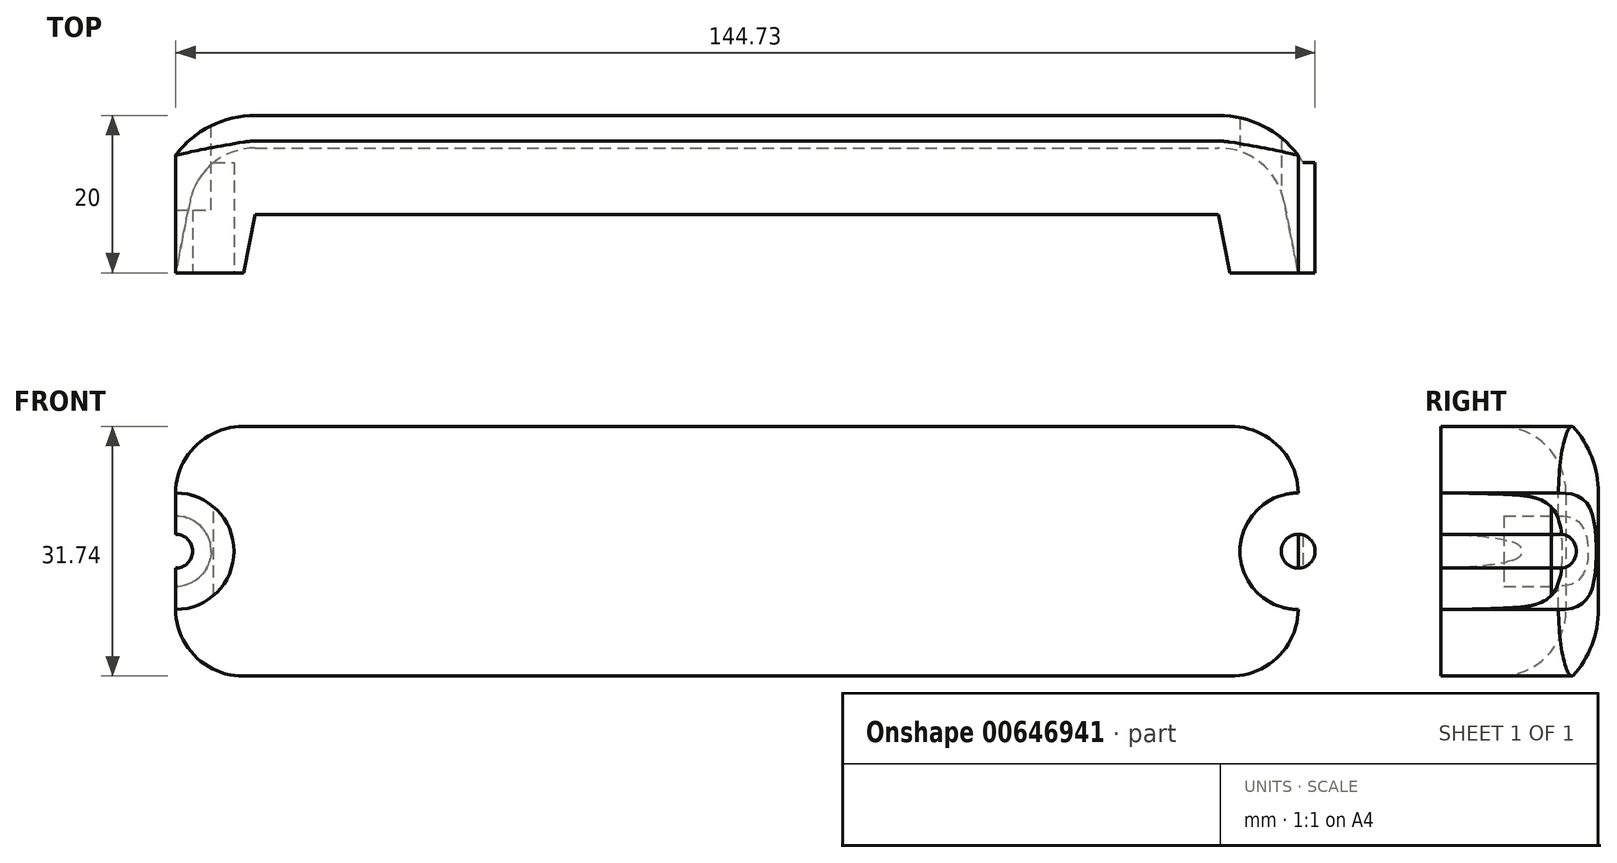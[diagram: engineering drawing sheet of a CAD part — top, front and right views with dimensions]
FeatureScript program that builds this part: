
annotation { "Feature Type Name" : "Feature", "Feature Type Description" : "" }
export const myFeature = defineFeature(function(context is Context, id is Id, definition is map)
    precondition{}
    {
        {
            var Q0;
            Q0=qCreatedBy(makeId("Top.planeOp"),FACE);
            var sketch = newSketch(context, id + "F0", { "sketchPlane" : qUnion([Q0])});
            skLineSegment(sketch, "E0.bottom", {"start": v(75.5, -10) * mm, "end": v(-75.5, -10) * mm});
            skLineSegment(sketch, "E0.top", {"start": v(75.5, 10) * mm, "end": v(-75.5, 10) * mm});
            skLineSegment(sketch, "E0.left", {"start": v(75.5, -10) * mm, "end": v(75.5, 10) * mm});
            skLineSegment(sketch, "E0.right", {"start": v(-75.5, -10) * mm, "end": v(-75.5, 10) * mm});
            skPoint(sketch, "E0.middle", {"position": v(0, 0) * mm});
            skLineSegment(sketch, "E1", {"start": v(-75.5, -10) * mm, "end": v(-71.52, 10) * mm});
            skLineSegment(sketch, "E2.MirrorCS", {"start": v(75.5, -10) * mm, "end": v(71.52, 10) * mm});
            skSolve(sketch);
        }
        {
            var Q0;
            Q0=makeQuery(id+"F0.imprint","IMPRINT",FACE,{"disambiguationData":[TD([[makeQuery(id+"F0.imprint","IMPRINT",EDGE,{"derivedFrom":sQuery(id+"F0.wireOp",EDGE,"E0.bottom")}),-1.0]])]});
            extrude(context, id + "F1", {"entities" : qUnion([Q0]), "depth" : 40 * mm, "offsetDistance" : 25 * mm});
        }
        {
            var Q0;
            Q0=makeQuery(id+"F1.opExtrude","SWEPT_EDGE",EDGE,{"disambiguationData":[OSD([sQuery(id+"F0.wireOp",EDGE,"E0.top"),sQuery(id+"F0.wireOp",EDGE,"E1")])]});
            var Q1;
            Q1=makeQuery(id+"F1.opExtrude","CAP_EDGE",EDGE,{"disambiguationData":[OSD([sQuery(id+"F0.wireOp",EDGE,"E0.top")])],"isStart":false});
            var Q2;
            Q2=makeQuery(id+"F1.opExtrude","CAP_EDGE",EDGE,{"disambiguationData":[OSD([sQuery(id+"F0.wireOp",EDGE,"E0.top")])],"isStart":true});
            var Q3;
            Q3=makeQuery(id+"F1.opExtrude","SWEPT_EDGE",EDGE,{"disambiguationData":[OSD([sQuery(id+"F0.wireOp",EDGE,"E0.top"),sQuery(id+"F0.wireOp",EDGE,"E2.MirrorCS")])]});
            var Q4;
            Q4=makeQuery(id+"F1.opExtrude","CAP_EDGE",EDGE,{"disambiguationData":[OSD([sQuery(id+"F0.wireOp",EDGE,"E1")])],"isStart":false});
            var Q5;
            Q5=makeQuery(id+"F1.opExtrude","CAP_EDGE",EDGE,{"disambiguationData":[OSD([sQuery(id+"F0.wireOp",EDGE,"E1")])],"isStart":true});
            var Q6;
            Q6=makeQuery(id+"F1.opExtrude","CAP_EDGE",EDGE,{"disambiguationData":[OSD([sQuery(id+"F0.wireOp",EDGE,"E2.MirrorCS")])],"isStart":false});
            var Q7;
            Q7=makeQuery(id+"F1.opExtrude","CAP_EDGE",EDGE,{"disambiguationData":[OSD([sQuery(id+"F0.wireOp",EDGE,"E2.MirrorCS")])],"isStart":true});
            fillet(context, id + "F2", {"entities" : qUnion([Q0, Q1, Q2, Q3, Q4, Q5, Q6, Q7]), "radius" : 12.6 * mm, "tangentPropagation" : true, "allowEdgeOverflow" : false});
        }
        {
            var Q0;
            Q0=makeQuery(id+"F1.opExtrude","SWEPT_FACE",FACE,{"disambiguationData":[OSD([sQuery(id+"F0.wireOp",EDGE,"E0.bottom")])]});
            var Q1;
            Q1=makeQuery(id+"F1.opExtrude","SWEPT_BODY",BODY,{"disambiguationData":[OSD([sQuery(id+"F0.wireOp",EDGE,"E0.bottom"),sQuery(id+"F0.wireOp",EDGE,"E0.top"),sQuery(id+"F0.wireOp",EDGE,"E1"),sQuery(id+"F0.wireOp",EDGE,"E2.MirrorCS")])]});
            shell(context, id + "F3", {"entities" : qUnion([Q0]), "parts" : qUnion([Q1]), "thickness" : 4.13 * mm});
        }
        {
            var Q0;
            Q0=makeQuery(id+"F1.opExtrude","SWEPT_FACE",FACE,{"disambiguationData":[OSD([sQuery(id+"F0.wireOp",EDGE,"E0.bottom")])]});
            var sketch = newSketch(context, id + "F4", { "sketchPlane" : qUnion([Q0])});
            skCircle(sketch, "E3", {"center": v(-71.3, 20) * mm, "radius": 2.15 * mm});
            skCircle(sketch, "E4.MirrorC", {"center": v(71.3, 20) * mm, "radius": 2.15 * mm});
            skPoint(sketch, "E5.startSnap0", {"position": v(-62.65, 25.2) * mm});
            skArc(sketch, "E6", {"start": v(-71.3, 27.4) * mm, "mid": v(-63.9, 20) * mm, "end": v(-71.3, 12.6) * mm});
            skArc(sketch, "E7", {"start": v(71.3, 27.4) * mm, "mid": v(63.9, 20) * mm, "end": v(71.3, 12.6) * mm});
            skSolve(sketch);
        }
        {
            var Q0;
            {var subQ0=sQuery(id+"F4.wireOp",EDGE,"E3");var subQ1=makeQuery(id+"F3.opShell","OFFSET_EDGE",EDGE,{"disambiguationData":[OSD([sQuery(id+"F0.wireOp",EDGE,"E0.bottom"),sQuery(id+"F0.wireOp",EDGE,"E0.right"),sQuery(id+"F0.wireOp",EDGE,"E1")])]});var subQ2=makeQuery(id+"F4.imprint","INTERSECT",VERTEX,{"disambiguationData":[OD(0.0)],"derivedFrom":[subQ1,subQ0]});Q0=makeQuery(id+"F4.imprint","IMPRINT",FACE,{"disambiguationData":[TD([[makeQuery(id+"F4.imprint","IMPRINT",EDGE,{"disambiguationData":[TD([[subQ2,-1.0]])],"derivedFrom":subQ0}),-1.0]])]});}
            var Q1;
            {var subQ0=sQuery(id+"F4.wireOp",EDGE,"E4.MirrorC");var subQ1=makeQuery(id+"F3.opShell","OFFSET_EDGE",EDGE,{"disambiguationData":[OSD([sQuery(id+"F0.wireOp",EDGE,"E0.bottom"),sQuery(id+"F0.wireOp",EDGE,"E0.left"),sQuery(id+"F0.wireOp",EDGE,"E2.MirrorCS")])]});var subQ2=makeQuery(id+"F4.imprint","INTERSECT",VERTEX,{"disambiguationData":[OD(0.0)],"derivedFrom":[subQ1,subQ0]});Q1=makeQuery(id+"F4.imprint","IMPRINT",FACE,{"disambiguationData":[TD([[makeQuery(id+"F4.imprint","IMPRINT",EDGE,{"disambiguationData":[TD([[subQ2,-1.0]])],"derivedFrom":subQ0}),1.0]])]});}
            extrude(context, id + "F5", {"entities" : qUnion([Q0, Q1]), "operationType" : NewBodyOperationType.ADD, "oppositeDirection" : true, "depth" : 14 * mm, "offsetDistance" : 25 * mm});
        }
        {
            var Q0;
            {var subQ0=sQuery(id+"F4.wireOp",EDGE,"E3");var subQ1=makeQuery(id+"F3.opShell","OFFSET_EDGE",EDGE,{"disambiguationData":[OSD([sQuery(id+"F0.wireOp",EDGE,"E0.bottom"),sQuery(id+"F0.wireOp",EDGE,"E0.right"),sQuery(id+"F0.wireOp",EDGE,"E1")])]});var subQ2=makeQuery(id+"F4.imprint","INTERSECT",VERTEX,{"disambiguationData":[OD(0.0)],"derivedFrom":[subQ1,subQ0]});Q0=makeQuery(id+"F4.imprint","IMPRINT",FACE,{"disambiguationData":[TD([[makeQuery(id+"F4.imprint","IMPRINT",EDGE,{"disambiguationData":[TD([[subQ2,-1.0]])],"derivedFrom":subQ0}),1.0]])]});}
            var Q1;
            {var subQ0=sQuery(id+"F4.wireOp",EDGE,"E3");var subQ1=makeQuery(id+"F3.opShell","OFFSET_EDGE",EDGE,{"disambiguationData":[OSD([sQuery(id+"F0.wireOp",EDGE,"E0.bottom"),sQuery(id+"F0.wireOp",EDGE,"E0.right"),sQuery(id+"F0.wireOp",EDGE,"E1")])]});var subQ2=makeQuery(id+"F4.imprint","INTERSECT",VERTEX,{"disambiguationData":[OD(0.0)],"derivedFrom":[subQ1,subQ0]});Q1=makeQuery(id+"F4.imprint","IMPRINT",FACE,{"disambiguationData":[TD([[makeQuery(id+"F4.imprint","IMPRINT",EDGE,{"disambiguationData":[TD([[subQ2,1.0]])],"derivedFrom":subQ0}),1.0]])]});}
            var Q2;
            {var subQ0=sQuery(id+"F4.wireOp",EDGE,"E4.MirrorC");var subQ1=makeQuery(id+"F3.opShell","OFFSET_EDGE",EDGE,{"disambiguationData":[OSD([sQuery(id+"F0.wireOp",EDGE,"E0.bottom"),sQuery(id+"F0.wireOp",EDGE,"E0.left"),sQuery(id+"F0.wireOp",EDGE,"E2.MirrorCS")])]});var subQ2=makeQuery(id+"F4.imprint","INTERSECT",VERTEX,{"disambiguationData":[OD(0.0)],"derivedFrom":[subQ1,subQ0]});Q2=makeQuery(id+"F4.imprint","IMPRINT",FACE,{"disambiguationData":[TD([[makeQuery(id+"F4.imprint","IMPRINT",EDGE,{"disambiguationData":[TD([[subQ2,-1.0]])],"derivedFrom":subQ0}),-1.0]])]});}
            var Q3;
            {var subQ0=sQuery(id+"F4.wireOp",EDGE,"E4.MirrorC");var subQ1=makeQuery(id+"F3.opShell","OFFSET_EDGE",EDGE,{"disambiguationData":[OSD([sQuery(id+"F0.wireOp",EDGE,"E0.bottom"),sQuery(id+"F0.wireOp",EDGE,"E0.left"),sQuery(id+"F0.wireOp",EDGE,"E2.MirrorCS")])]});var subQ2=makeQuery(id+"F4.imprint","INTERSECT",VERTEX,{"disambiguationData":[OD(0.0)],"derivedFrom":[subQ1,subQ0]});Q3=makeQuery(id+"F4.imprint","IMPRINT",FACE,{"disambiguationData":[TD([[makeQuery(id+"F4.imprint","IMPRINT",EDGE,{"disambiguationData":[TD([[subQ2,1.0]])],"derivedFrom":subQ0}),-1.0]])]});}
            extrude(context, id + "F6", {"entities" : qUnion([Q0, Q1, Q2, Q3]), "operationType" : NewBodyOperationType.REMOVE, "endBound" : BoundingType.THROUGH_ALL, "oppositeDirection" : true, "depth" : 25 * mm, "offsetDistance" : 25 * mm});
        }
        {
            var Q0;
            Q0=makeQuery(id+"F1.opExtrude","SWEPT_FACE",FACE,{"disambiguationData":[OSD([sQuery(id+"F0.wireOp",EDGE,"E0.top")])]});
            var sketch = newSketch(context, id + "F7", { "sketchPlane" : qUnion([Q0])});
            skCircle(sketch, "E8", {"center": v(71.27, 20.01) * mm, "radius": 4.47 * mm});
            skCircle(sketch, "E9.MirrorC", {"center": v(-71.27, 20.01) * mm, "radius": 4.47 * mm});
            skSolve(sketch);
        }
        {
            var Q0;
            Q0=makeQuery(id+"F7.imprint","IMPRINT",FACE,{"disambiguationData":[TD([[makeQuery(id+"F7.imprint","IMPRINT",EDGE,{"derivedFrom":sQuery(id+"F7.wireOp",EDGE,"E8")}),1.0]])]});
            var Q1;
            Q1=makeQuery(id+"F7.imprint","IMPRINT",FACE,{"disambiguationData":[TD([[makeQuery(id+"F7.imprint","IMPRINT",EDGE,{"derivedFrom":sQuery(id+"F7.wireOp",EDGE,"E9.MirrorC")}),-1.0]])]});
            extrude(context, id + "F8", {"entities" : qUnion([Q0, Q1]), "operationType" : NewBodyOperationType.REMOVE, "oppositeDirection" : true, "depth" : 12 * mm, "offsetDistance" : 25 * mm});
        }
    });
